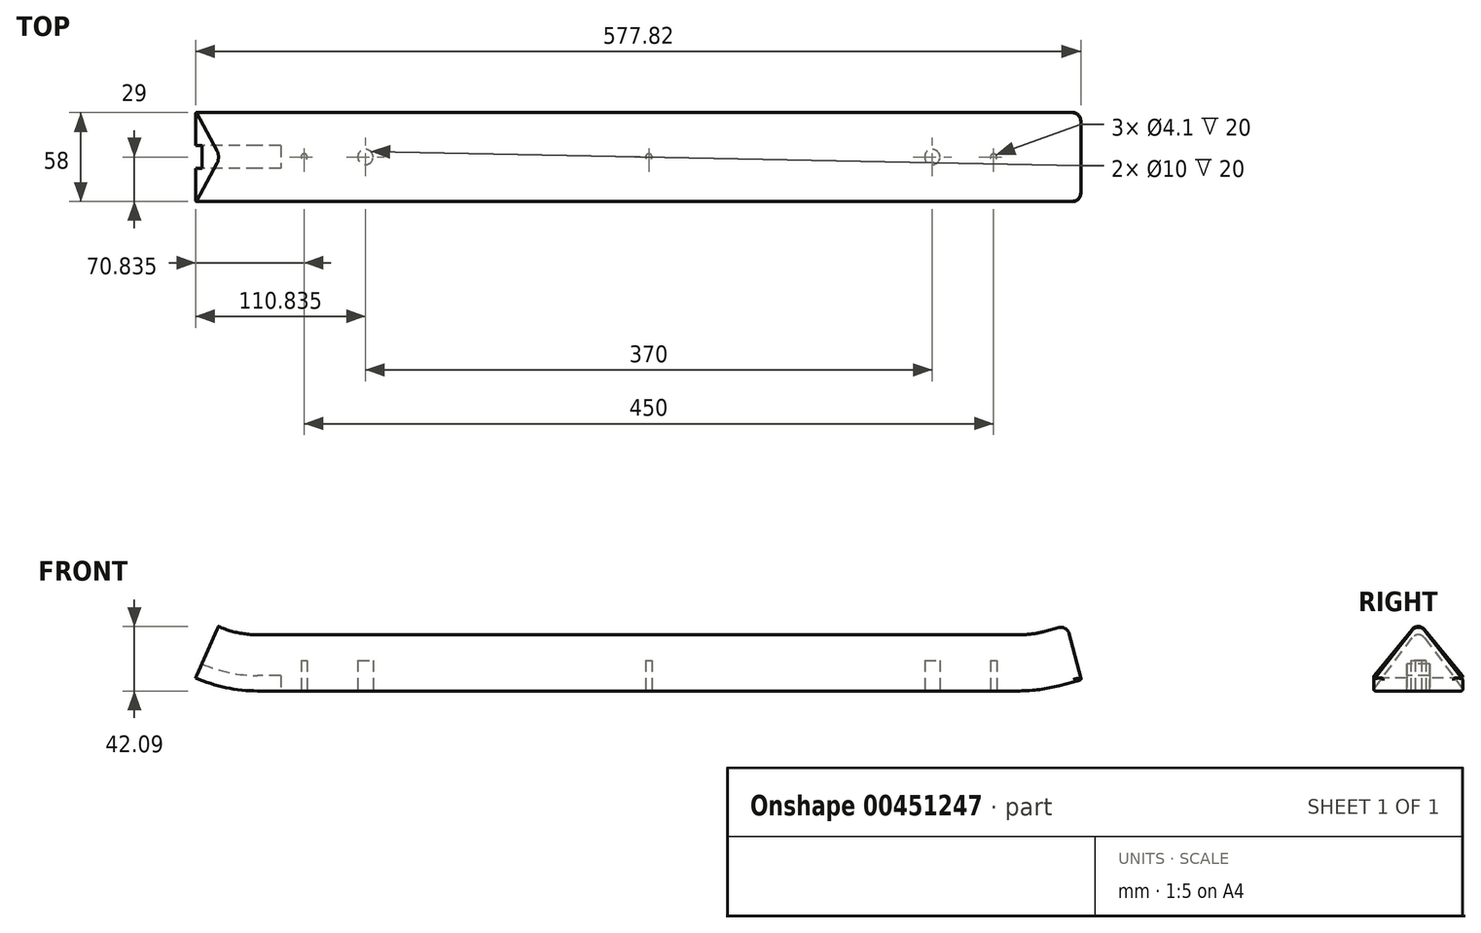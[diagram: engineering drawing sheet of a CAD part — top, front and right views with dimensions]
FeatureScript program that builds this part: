
annotation { "Feature Type Name" : "Feature", "Feature Type Description" : "" }
export const myFeature = defineFeature(function(context is Context, id is Id, definition is map)
    precondition{}
    {
        {
            var Q0;
            Q0=qCreatedBy(makeId("Right.planeOp"),FACE);
            var sketch = newSketch(context, id + "F0", { "sketchPlane" : qUnion([Q0])});
            skLineSegment(sketch, "E0", {"start": v(30, 0) * mm, "end": v(-30, 0) * mm});
            skLineSegment(sketch, "E1", {"start": v(-30, 0) * mm, "end": v(0, 40) * mm});
            skLineSegment(sketch, "E2", {"start": v(0, 40) * mm, "end": v(30, 0) * mm});
            skSolve(sketch);
        }
        {
            var Q0;
            Q0=qCreatedBy(makeId("Front.planeOp"),FACE);
            var sketch = newSketch(context, id + "F1", { "sketchPlane" : qUnion([Q0])});
            skLineSegment(sketch, "E3", {"start": v(0, 0) * mm, "end": v(486.83, 0) * mm});
            skLineSegment(sketch, "E4", {"start": v(512.72, 3.4) * mm, "end": v(527.05, 7.25) * mm});
            skPoint(sketch, "E5.visualSharp", {"position": v(500, 0) * mm});
            skArc(sketch, "E5.filletArc", {"start": v(486.83, 0) * mm, "mid": v(499.89, 0.86) * mm, "end": v(512.72, 3.4) * mm});
            skLineSegment(sketch, "E6", {"start": v(0, 0) * mm, "end": v(-10.5, 0) * mm});
            skArc(sketch, "E7.filletArc", {"start": v(-51, 8.57) * mm, "mid": v(-31.2, 2.17) * mm, "end": v(-10.5, 0) * mm});
            skSolve(sketch);
        }
        {
            var Q0;
            Q0=qSketchRegion(id+"F0",true);
            var Q1;
            Q1=sQuery(id+"F1.wireOp",EDGE,"hpb3y6mx-TUyL-NVhM-2wwJ-ZHGj73JeWUuP");
            var Q2;
            Q2=sQuery(id+"F1.wireOp",EDGE,"c73ef651-b25a-4fa9-a172-00b2d057481d.filletArc");
            var Q3;
            Q3=sQuery(id+"F1.wireOp",EDGE,"4lItoZta-QgLP-WyET-9Vek-mWAvu2dLh5lC");
            var Q4;
            Q4=sQuery(id+"F1.wireOp",EDGE,"E3");
            var Q5;
            Q5=sQuery(id+"F1.wireOp",EDGE,"E5.filletArc");
            var Q6;
            Q6=sQuery(id+"F1.wireOp",EDGE,"E4");
            var Q7;
            Q7=sQuery(id+"F1.wireOp",EDGE,"E6");
            var Q8;
            Q8=sQuery(id+"F1.wireOp",EDGE,"E7.filletArc");
            var Q9;
            Q9=sQuery(id+"F1.wireOp",EDGE,"3a3gwADy-TxzK-0xbG-qDqz-4KbkflDc9CcQ");
            sweep(context, id + "F2", {"profiles" : qUnion([Q0]), "path" : qUnion([Q1, Q2, Q3, Q4, Q5, Q6, Q7, Q8, Q9])});
        }
        {
            var Q0;
            Q0=makeQuery(id+"F2.opSweep","SWEPT_EDGE",EDGE,{"disambiguationData":[OSD([sQuery(id+"F0.wireOp",EDGE,"E1"),sQuery(id+"F0.wireOp",EDGE,"E2"),sQuery(id+"F1.wireOp",EDGE,"hpb3y6mx-TUyL-NVhM-2wwJ-ZHGj73JeWUuP")])]});
            fillet(context, id + "F3", {"entities" : qUnion([Q0]), "tangentPropagation" : true, "radius" : 5 * mm, "defaultsChanged" : true, "vertexSettings" : [], "allowEdgeOverflow" : false});
        }
        {
            var Q0;
            Q0=makeQuery(id+"F2.opSweep","SWEPT_FACE",FACE,{"disambiguationData":[OSD([sQuery(id+"F0.wireOp",EDGE,"E0"),sQuery(id+"F1.wireOp",EDGE,"E6")])]});
            var sketch = newSketch(context, id + "F4", { "sketchPlane" : qUnion([Q0])});
            skCircle(sketch, "E8", {"center": v(469.83, 0) * mm, "radius": 2.05 * mm});
            skCircle(sketch, "E9", {"center": v(429.83, 0) * mm, "radius": 5 * mm});
            skCircle(sketch, "E10", {"center": v(59.83, 0) * mm, "radius": 5 * mm});
            skCircle(sketch, "E11", {"center": v(19.83, 0) * mm, "radius": 2.05 * mm});
            skCircle(sketch, "E12", {"center": v(244.83, 0) * mm, "radius": 2.05 * mm});
            skSolve(sketch);
        }
        {
            var Q0;
            Q0 = qSketchRegion(id + "F4", true);
            extrude(context, id + "F5", {"entities" : qUnion([Q0]), "operationType" : NewBodyOperationType.REMOVE, "oppositeDirection" : true, "depth" : 20 * mm, "offsetDistance" : 25 * mm});
        }
        {
            var Q0;
            Q0=makeQuery(id+"F2.opSweep","SWEPT_FACE",FACE,{"disambiguationData":[OSD([sQuery(id+"F0.wireOp",EDGE,"E0"),sQuery(id+"F1.wireOp",EDGE,"E6")])]});
            var sketch = newSketch(context, id + "F6", { "sketchPlane" : qUnion([Q0])});
            skLineSegment(sketch, "E13.bottom", {"start": v(4.5, -7.5) * mm, "end": v(-10.5, -7.5) * mm});
            skLineSegment(sketch, "E13.top", {"start": v(4.5, 7.5) * mm, "end": v(-10.5, 7.5) * mm});
            skLineSegment(sketch, "E13.left", {"start": v(4.5, -7.5) * mm, "end": v(4.5, 7.5) * mm});
            skLineSegment(sketch, "E13.right", {"start": v(-10.5, -7.5) * mm, "end": v(-10.5, 7.5) * mm});
            skPoint(sketch, "E13.middle", {"position": v(-3, 0) * mm});
            skSolve(sketch);
        }
        {
            var Q0;
            Q0 = qSketchRegion(id + "F6", true);
            extrude(context, id + "F7", {"entities" : qUnion([Q0]), "operationType" : NewBodyOperationType.REMOVE, "oppositeDirection" : true, "depth" : 10 * mm, "offsetDistance" : 25 * mm});
        }
        {
            var Q0;
            Q0=makeQuery(id+"F7.boolean.opBoolean","COPY",FACE,{"derivedFrom":makeQuery(id+"F7.opExtrude","SWEPT_FACE",FACE,{"disambiguationData":[OSD([sQuery(id+"F6.wireOp",EDGE,"E13.right")])]})});
            var Q1;
            Q1=makeQuery(id+"F2.opSweep","SWEPT_EDGE",EDGE,{"disambiguationData":[OSD([sQuery(id+"F0.wireOp",EDGE,"E0"),sQuery(id+"F0.wireOp",EDGE,"E1"),sQuery(id+"F1.wireOp",EDGE,"E7.filletArc")])]});
            sweep(context, id + "F8", {"operationType" : NewBodyOperationType.REMOVE, "profiles" : qUnion([Q0]), "path" : qUnion([Q1])});
        }
        {
            var Q0;
            Q0=makeQuery(id+"F2.opSweep","CAP_EDGE",EDGE,{"disambiguationData":[OSD([sQuery(id+"F0.wireOp",EDGE,"E2"),sQuery(id+"F1.wireOp",VERTEX,"E4.end")])],"isStart":false});
            fillet(context, id + "F9", {"entities" : qUnion([Q0]), "tangentPropagation" : true, "radius" : 5 * mm, "defaultsChanged" : false, "vertexSettings" : [], "allowEdgeOverflow" : false});
        }
        {
            var Q0;
            Q0=makeQuery(id+"F2.opSweep","SWEPT_EDGE",EDGE,{"disambiguationData":[OSD([sQuery(id+"F0.wireOp",EDGE,"E0"),sQuery(id+"F0.wireOp",EDGE,"E2"),sQuery(id+"F1.wireOp",EDGE,"E6")])]});
            fillet(context, id + "F10", {"entities" : qUnion([Q0]), "tangentPropagation" : true, "radius" : 1 * mm, "defaultsChanged" : false, "vertexSettings" : [], "allowEdgeOverflow" : false});
        }
    });
